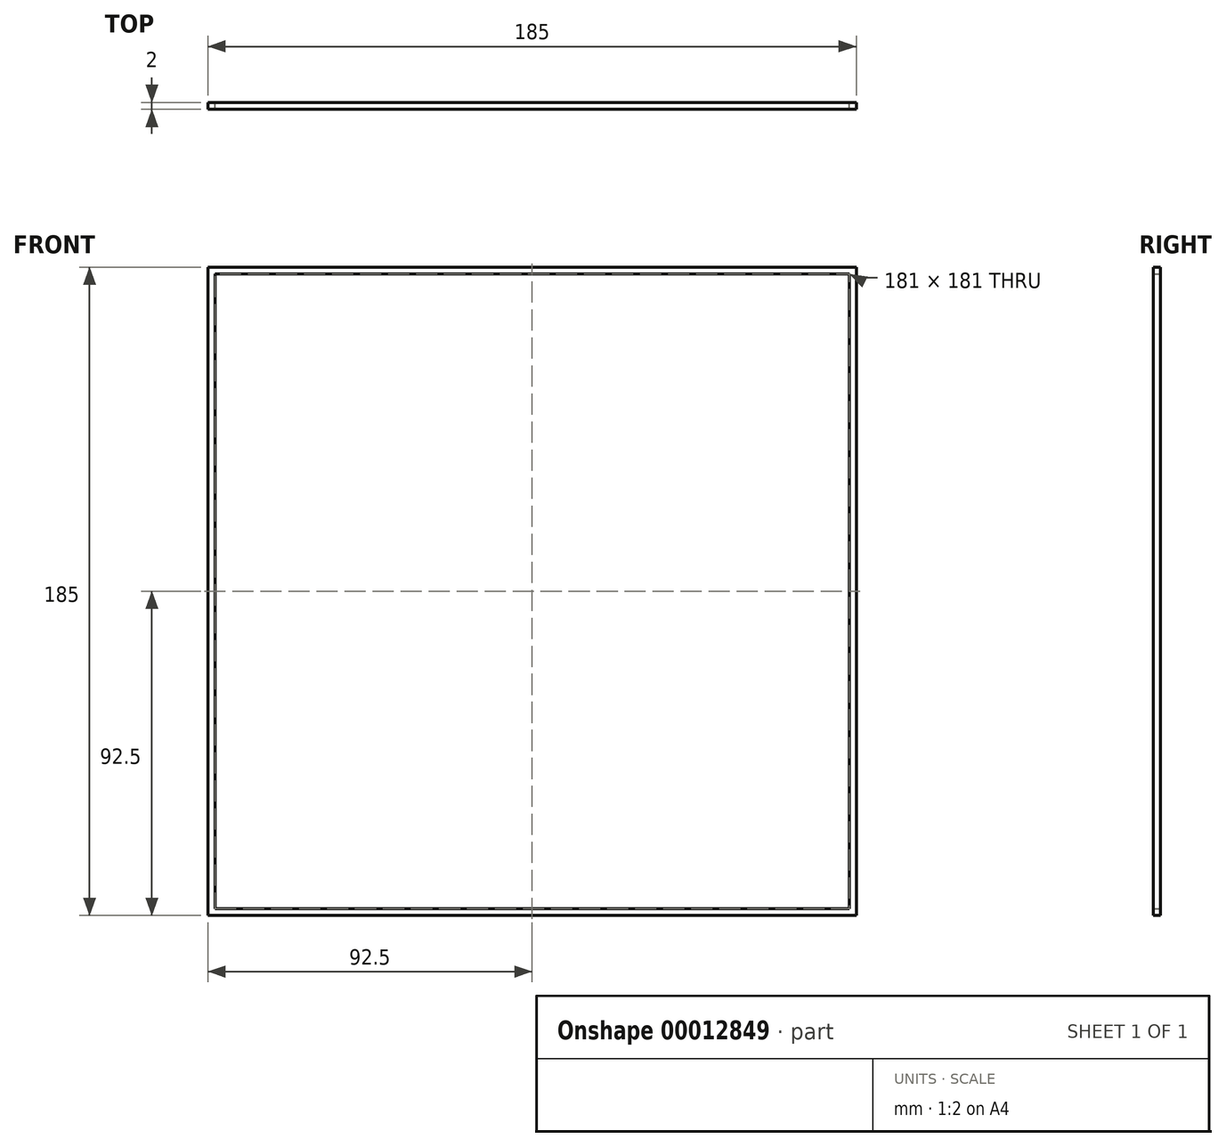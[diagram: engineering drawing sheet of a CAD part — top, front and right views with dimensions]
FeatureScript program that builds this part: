
annotation { "Feature Type Name" : "Feature", "Feature Type Description" : "" }
export const myFeature = defineFeature(function(context is Context, id is Id, definition is map)
    precondition{}
    {
        {
            var Q0;
            Q0=qCreatedBy(makeId("Front.planeOp"),FACE);
            var sketch = newSketch(context, id + "F1", { "sketchPlane" : qUnion([Q0])});
            skLineSegment(sketch, "E0.rect.bottom", {"start": v(0, 0) * mm, "end": v(0, 0) * mm});
            skLineSegment(sketch, "E0.rect.top", {"start": v(0, 0) * mm, "end": v(0, 0) * mm});
            skLineSegment(sketch, "E0.rect.left", {"start": v(0, 0) * mm, "end": v(0, 0) * mm});
            skLineSegment(sketch, "E0.rect.right", {"start": v(0, 0) * mm, "end": v(0, 0) * mm});
            skPoint(sketch, "E0.rect.middle", {"position": v(0, 0) * mm});
            skLineSegment(sketch, "E1.rect.bottom", {"start": v(92.5, 92.5) * mm, "end": v(-92.5, 92.5) * mm});
            skLineSegment(sketch, "E1.rect.top", {"start": v(92.5, -92.5) * mm, "end": v(-92.5, -92.5) * mm});
            skLineSegment(sketch, "E1.rect.left", {"start": v(92.5, 92.5) * mm, "end": v(92.5, -92.5) * mm});
            skLineSegment(sketch, "E1.rect.right", {"start": v(-92.5, 92.5) * mm, "end": v(-92.5, -92.5) * mm});
            skLineSegment(sketch, "E2.0", {"start": v(90.5, -90.5) * mm, "end": v(-90.5, -90.5) * mm});
            skLineSegment(sketch, "E2.1", {"start": v(90.5, 90.5) * mm, "end": v(90.5, -90.5) * mm});
            skLineSegment(sketch, "E2.2", {"start": v(90.5, 90.5) * mm, "end": v(-90.5, 90.5) * mm});
            skLineSegment(sketch, "E2.3", {"start": v(-90.5, 90.5) * mm, "end": v(-90.5, -90.5) * mm});
            skSolve(sketch);
        }
        {
            var Q0;
            Q0=makeQuery(id+"F1.imprint","IMPRINT",FACE,{"disambiguationData":[TD([[makeQuery(id+"F1.imprint","IMPRINT",EDGE,{"derivedFrom":sQuery(id+"F1.wireOp",EDGE,"E1.rect.bottom")}),1.0]])]});
            extrude(context, id + "F0", {"entities" : qUnion([Q0]), "depth" : 2 * mm});
        }
    });
